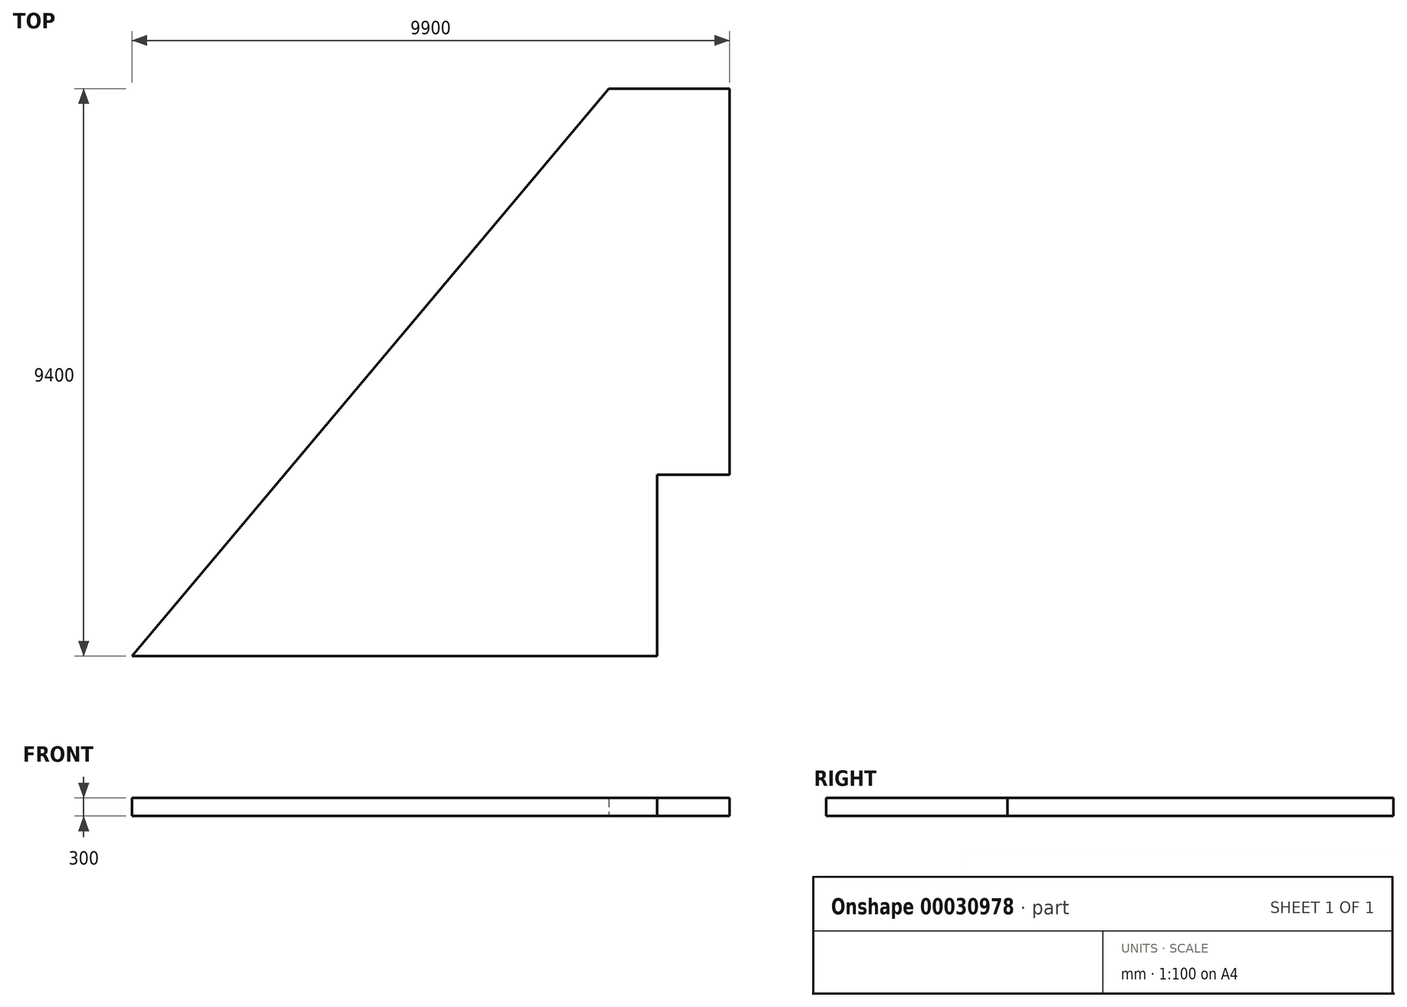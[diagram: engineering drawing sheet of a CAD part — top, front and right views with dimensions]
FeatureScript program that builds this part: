
annotation { "Feature Type Name" : "Feature", "Feature Type Description" : "" }
export const myFeature = defineFeature(function(context is Context, id is Id, definition is map)
    precondition{}
    {
        {
            var Q0;
            Q0=qCreatedBy(makeId("Top.planeOp"),FACE);
            var sketch = newSketch(context, id + "F0", { "sketchPlane" : qUnion([Q0])});
            skLineSegment(sketch, "E0", {"start": v(0, 0) * mm, "end": v(0, 9400) * mm});
            skLineSegment(sketch, "E1", {"start": v(0, 9400) * mm, "end": v(-2000, 9400) * mm});
            skLineSegment(sketch, "E2", {"start": v(-2000, 9400) * mm, "end": v(-9900, 0) * mm});
            skLineSegment(sketch, "E3", {"start": v(-9900, 0) * mm, "end": v(0, 0) * mm});
            skSolve(sketch);
        }
        {
            var Q0;
            Q0=makeQuery(id+"F0.imprint","IMPRINT",FACE,{"disambiguationData":[TD([[makeQuery(id+"F0.imprint","IMPRINT",EDGE,{"derivedFrom":sQuery(id+"F0.wireOp",EDGE,"E0")}),1.0]])]});
            extrude(context, id + "F1", {"entities" : qUnion([Q0]), "depth" : 300 * mm});
        }
        {
            var Q0;
            Q0=makeQuery(id+"F1.opExtrude","CAP_FACE",FACE,{"disambiguationData":[OSD([sQuery(id+"F0.wireOp",EDGE,"E0"),sQuery(id+"F0.wireOp",EDGE,"E1"),sQuery(id+"F0.wireOp",EDGE,"E2"),sQuery(id+"F0.wireOp",EDGE,"E3")])],"isStart":false});
            var sketch = newSketch(context, id + "F2", { "sketchPlane" : qUnion([Q0])});
            skLineSegment(sketch, "E4.bottom", {"start": v(0, 0) * mm, "end": v(-1200, 0) * mm});
            skLineSegment(sketch, "E4.top", {"start": v(0, 3003.15) * mm, "end": v(-1200, 3003.15) * mm});
            skLineSegment(sketch, "E4.left", {"start": v(0, 0) * mm, "end": v(0, 3003.15) * mm});
            skLineSegment(sketch, "E4.right", {"start": v(-1200, 0) * mm, "end": v(-1200, 3003.15) * mm});
            skSolve(sketch);
        }
        {
            var Q0;
            Q0=makeQuery(id+"F2.imprint","IMPRINT",FACE,{"disambiguationData":[TD([[makeQuery(id+"F2.imprint","IMPRINT",EDGE,{"derivedFrom":sQuery(id+"F2.wireOp",EDGE,"E4.bottom")}),1.0]])]});
            extrude(context, id + "F3", {"entities" : qUnion([Q0]), "operationType" : NewBodyOperationType.REMOVE, "endBound" : BoundingType.THROUGH_ALL, "oppositeDirection" : true, "depth" : 25 * mm});
        }
    });
